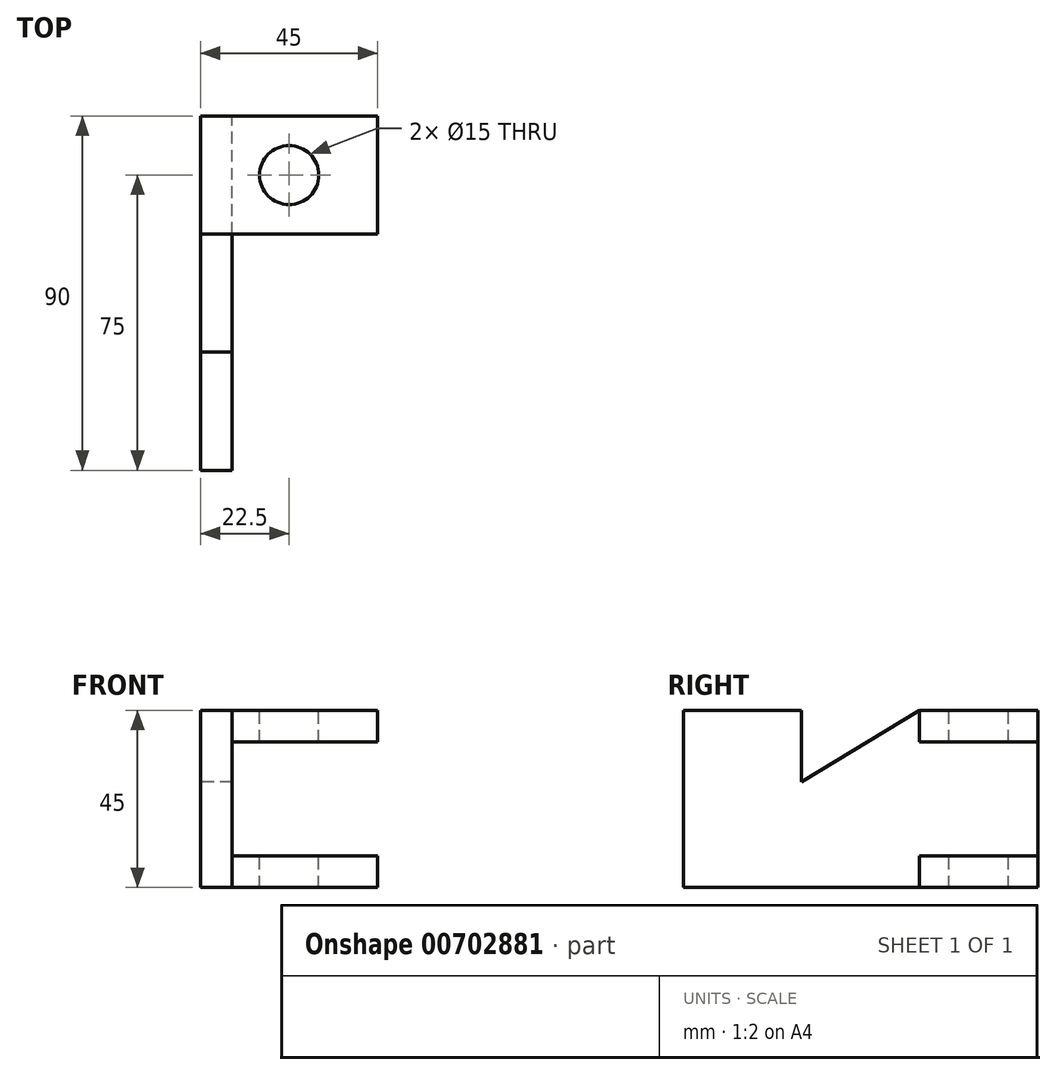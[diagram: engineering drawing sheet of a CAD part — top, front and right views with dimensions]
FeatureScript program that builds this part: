
annotation { "Feature Type Name" : "Feature", "Feature Type Description" : "" }
export const myFeature = defineFeature(function(context is Context, id is Id, definition is map)
    precondition{}
    {
        {
            var Q0;
            Q0=qCreatedBy(makeId("Right.planeOp"),FACE);
            var sketch = newSketch(context, id + "F0", { "sketchPlane" : qUnion([Q0])});
            skLineSegment(sketch, "E0", {"start": v(0, 0) * mm, "end": v(90, 0) * mm});
            skLineSegment(sketch, "E1", {"start": v(60, 45) * mm, "end": v(30, 26.85) * mm});
            skLineSegment(sketch, "E2", {"start": v(30, 26.85) * mm, "end": v(30, 45) * mm});
            skLineSegment(sketch, "E3", {"start": v(30, 45) * mm, "end": v(0, 45) * mm});
            skLineSegment(sketch, "E4", {"start": v(0, 45) * mm, "end": v(0, 0) * mm});
            skLineSegment(sketch, "E5", {"start": v(90, 0) * mm, "end": v(90, 45) * mm});
            skLineSegment(sketch, "E6", {"start": v(90, 45) * mm, "end": v(60, 45) * mm});
            skSolve(sketch);
        }
        {
            var Q0;
            Q0 = qSketchRegion(id + "F0", true);
            extrude(context, id + "F1", {"entities" : qUnion([Q0]), "depth" : 8 * mm, "offsetDistance" : 25.4 * mm});
        }
        {
            var Q0;
            Q0=makeQuery(id+"F1.opExtrude","CAP_FACE",FACE,{"disambiguationData":[OSD([sQuery(id+"F0.wireOp",EDGE,"E0"),sQuery(id+"F0.wireOp",EDGE,"E1"),sQuery(id+"F0.wireOp",EDGE,"E2"),sQuery(id+"F0.wireOp",EDGE,"E3"),sQuery(id+"F0.wireOp",EDGE,"E4"),sQuery(id+"F0.wireOp",EDGE,"E5"),sQuery(id+"F0.wireOp",EDGE,"E6")])],"isStart":false});
            var sketch = newSketch(context, id + "F2", { "sketchPlane" : qUnion([Q0])});
            skLineSegment(sketch, "E7", {"start": v(60, 45) * mm, "end": v(60, 37) * mm});
            skLineSegment(sketch, "E8", {"start": v(60, 37) * mm, "end": v(90, 37) * mm});
            skLineSegment(sketch, "E9", {"start": v(60, 0) * mm, "end": v(60, 8) * mm});
            skLineSegment(sketch, "E10", {"start": v(60, 8) * mm, "end": v(90, 8) * mm});
            skLineSegment(sketch, "E11", {"start": v(90, 37) * mm, "end": v(90, 45) * mm});
            skLineSegment(sketch, "E12", {"start": v(90, 45) * mm, "end": v(60, 45) * mm});
            skLineSegment(sketch, "E13", {"start": v(60, 0) * mm, "end": v(90, 0) * mm});
            skLineSegment(sketch, "E14", {"start": v(90, 0) * mm, "end": v(90, 8) * mm});
            skSolve(sketch);
        }
        {
            var Q0;
            Q0 = qSketchRegion(id + "F2", true);
            extrude(context, id + "F3", {"entities" : qUnion([Q0]), "operationType" : NewBodyOperationType.ADD, "depth" : 37 * mm, "offsetDistance" : 25.4 * mm});
        }
        {
            var Q0;
            Q0=makeQuery(id+"F3.boolean.opBoolean","MERGE",FACE,{"derivedFrom":[makeQuery(id+"F1.opExtrude","SWEPT_FACE",FACE,{"disambiguationData":[OSD([sQuery(id+"F0.wireOp",EDGE,"E6")])]}),makeQuery(id+"F3.opExtrude","SWEPT_FACE",FACE,{"disambiguationData":[OSD([sQuery(id+"F2.wireOp",EDGE,"E12")])]})]});
            var sketch = newSketch(context, id + "F4", { "sketchPlane" : qUnion([Q0])});
            skCircle(sketch, "E15", {"center": v(22.5, 75) * mm, "radius": 7.5 * mm});
            skSolve(sketch);
        }
        {
            var Q0;
            Q0 = qSketchRegion(id + "F4", true);
            extrude(context, id + "F5", {"entities" : qUnion([Q0]), "operationType" : NewBodyOperationType.REMOVE, "endBound" : BoundingType.THROUGH_ALL, "oppositeDirection" : true, "depth" : 25.4 * mm, "offsetDistance" : 25.4 * mm});
        }
    });
